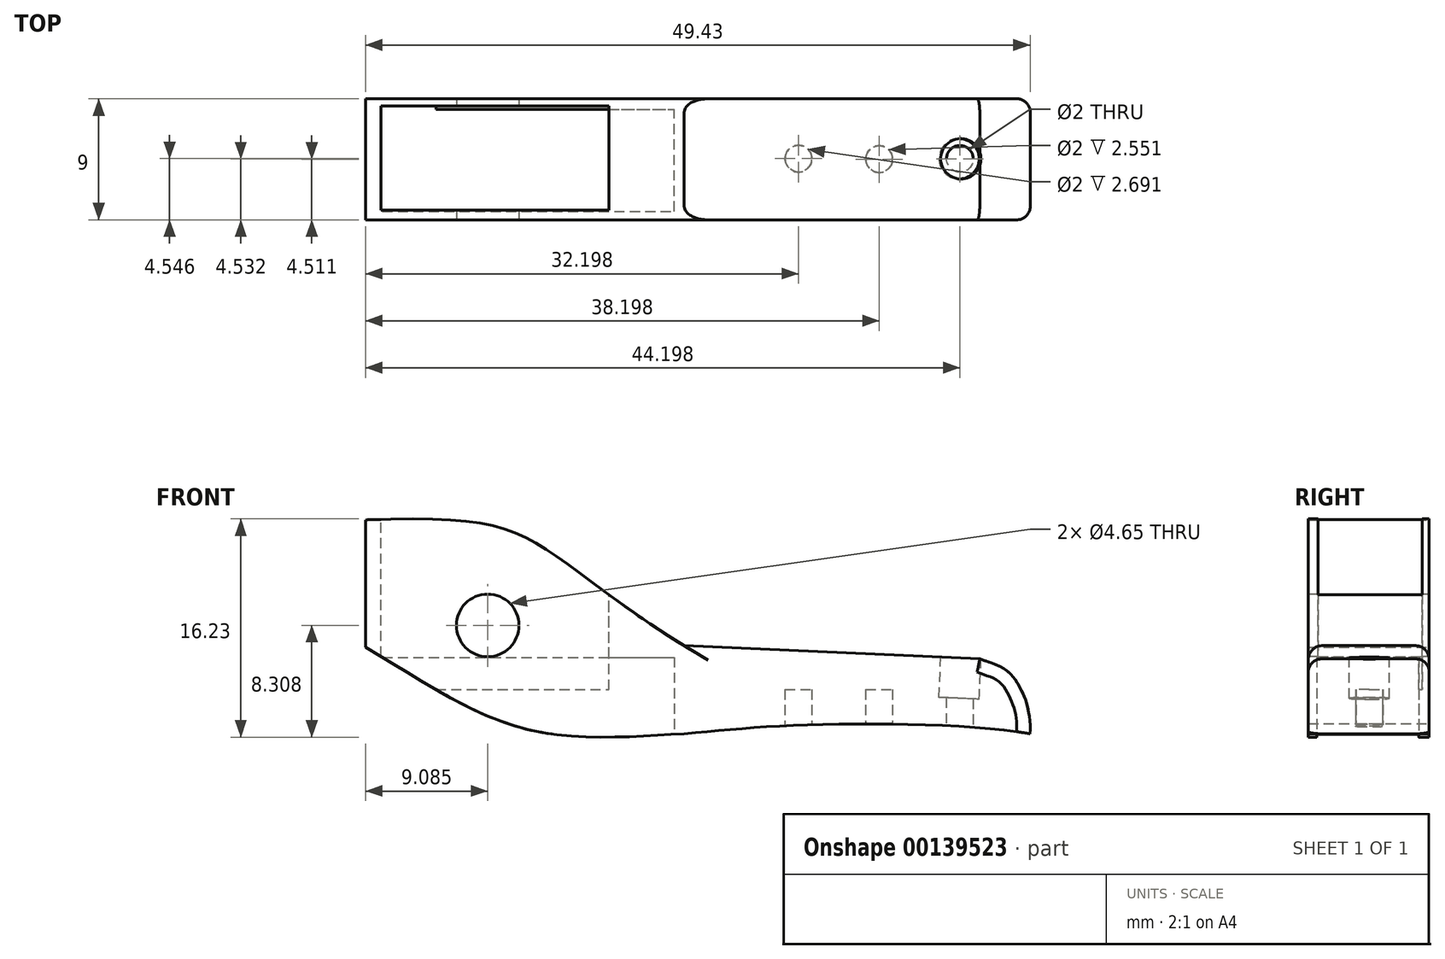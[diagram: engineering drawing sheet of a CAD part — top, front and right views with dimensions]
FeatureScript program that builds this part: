
annotation { "Feature Type Name" : "Feature", "Feature Type Description" : "" }
export const myFeature = defineFeature(function(context is Context, id is Id, definition is map)
    precondition{}
    {
        {
            var Q0;
            Q0=qCreatedBy(makeId("Front.planeOp"),FACE);
            var sketch = newSketch(context, id + "F0", { "sketchPlane" : qUnion([Q0])});
            skLineSegment(sketch, "E0", {"start": v(-18.11, 14.62) * mm, "end": v(-18.11, 5.15) * mm});
            skFitSpline(sketch, "E1", {"points": [v(-18.11, 14.62) * mm, v(-5.7, 13.04) * mm, v(5.6, 5.26) * mm], "startDerivative": vector(43.3, 1.46) * mm, "endDerivative": vector(32.79, -20.12) * mm});
            skFitSpline(sketch, "E2", {"points": [v(-18.11, 5.15) * mm, v(-6.1, -0.96) * mm, v(5.6, -1.29) * mm], "startDerivative": vector(24.76, -14.65) * mm, "endDerivative": vector(22.2, 1.12) * mm});
            skLineSegment(sketch, "E3", {"start": v(-5.7, 13.04) * mm, "end": v(-6.1, -0.96) * mm, "construction": true});
            skFitSpline(sketch, "E4", {"points": [v(5.6, -1.29) * mm, v(15.63, -0.6) * mm, v(31.3, -1.29) * mm], "startDerivative": vector(20.89, 1.84) * mm, "endDerivative": vector(17.9, -3.47) * mm});
            skLineSegment(sketch, "E5", {"start": v(5.6, 5.26) * mm, "end": v(27.57, 4.28) * mm});
            skFitSpline(sketch, "E6", {"points": [v(27.57, 4.28) * mm, v(30.02, 2.98) * mm, v(31.3, -1.29) * mm], "startDerivative": vector(8.93, -3.19) * mm, "endDerivative": vector(-1.08, -8.77) * mm});
            skLineSegment(sketch, "E7", {"start": v(-18.11, 14.62) * mm, "end": v(31.89, 14.62) * mm, "construction": true});
            skLineSegment(sketch, "E8", {"start": v(31.89, 14.62) * mm, "end": v(31.3, -1.29) * mm, "construction": true});
            skSolve(sketch);
        }
        {
            var Q0;
            Q0=qSketchRegion(id+"F0",true);
            extrude(context, id + "F1", {"entities" : qUnion([Q0]), "depth" : 9 * mm});
        }
        {
            var Q0;
            Q0=makeQuery(id+"F1.opExtrude","CAP_FACE",FACE,{"disambiguationData":[OSD([sQuery(id+"F0.wireOp",EDGE,"E0"),sQuery(id+"F0.wireOp",EDGE,"E1"),sQuery(id+"F0.wireOp",EDGE,"E2"),sQuery(id+"F0.wireOp",EDGE,"E4"),sQuery(id+"F0.wireOp",EDGE,"E5"),sQuery(id+"F0.wireOp",EDGE,"E6")])],"isStart":false});
            var sketch = newSketch(context, id + "F2", { "sketchPlane" : qUnion([Q0])});
            skCircle(sketch, "E9", {"center": v(-9.02, 6.77) * mm, "radius": 2.32 * mm});
            skSolve(sketch);
        }
        {
            var Q0;
            Q0=qSketchRegion(id+"F2",true);
            extrude(context, id + "F3", {"entities" : qUnion([Q0]), "operationType" : NewBodyOperationType.REMOVE, "oppositeDirection" : true, "depth" : 25 * mm});
        }
        {
            var Q0;
            Q0=makeQuery(id+"F1.opExtrude","CAP_EDGE",EDGE,{"disambiguationData":[OSD([sQuery(id+"F0.wireOp",EDGE,"E5")])],"isStart":false});
            var Q1;
            Q1=makeQuery(id+"F1.opExtrude","CAP_EDGE",EDGE,{"disambiguationData":[OSD([sQuery(id+"F0.wireOp",EDGE,"E5")])],"isStart":true});
            var Q2;
            Q2=makeQuery(id+"F1.opExtrude","CAP_EDGE",EDGE,{"disambiguationData":[OSD([sQuery(id+"F0.wireOp",EDGE,"E6")])],"isStart":false});
            var Q3;
            Q3=makeQuery(id+"F1.opExtrude","CAP_EDGE",EDGE,{"disambiguationData":[OSD([sQuery(id+"F0.wireOp",EDGE,"E6")])],"isStart":true});
            fillet(context, id + "F4", {"entities" : qUnion([Q0, Q1, Q2, Q3]), "radius" : 1 * mm, "tangentPropagation" : true, "allowEdgeOverflow" : false});
        }
        {
            var Q0;
            Q0=qCreatedBy(makeId("Top.planeOp"),FACE);
            cPlane(context, id + "F5", {"entities" : qUnion([Q0]), "cplaneType" : CPlaneType.OFFSET, "offset" : 3 * mm, "oppositeDirection" : true, "width" : 150 * mm, "height" : 150 * mm});
        }
        {
            var Q0;
            Q0=qCreatedBy(id+"F5.planeOp",FACE);
            cPlane(context, id + "F6", {"entities" : qUnion([Q0]), "cplaneType" : CPlaneType.OFFSET, "offset" : 25 * mm, "width" : 150 * mm, "height" : 150 * mm});
        }
        {
            var Q0;
            Q0=qCreatedBy(id+"F5.planeOp",FACE);
            var sketch = newSketch(context, id + "F7", { "sketchPlane" : qUnion([Q0])});
            skLineSegment(sketch, "E10.bottom", {"start": v(-17.4, -8.37) * mm, "end": v(4.86, -8.37) * mm});
            skLineSegment(sketch, "E10.top", {"start": v(-17.4, -0.78) * mm, "end": v(4.86, -0.78) * mm});
            skLineSegment(sketch, "E10.left", {"start": v(-17.4, -8.37) * mm, "end": v(-17.4, -0.78) * mm});
            skLineSegment(sketch, "E10.right", {"start": v(4.86, -8.37) * mm, "end": v(4.86, -0.78) * mm});
            skSolve(sketch);
        }
        {
            var Q0;
            Q0 = qSketchRegion(id + "F7", true);
            extrude(context, id + "F8", {"entities" : qUnion([Q0]), "operationType" : NewBodyOperationType.REMOVE, "depth" : 7.4 * mm});
        }
        {
            var Q0;
            Q0=qCreatedBy(id+"F6.planeOp",FACE);
            var sketch = newSketch(context, id + "F9", { "sketchPlane" : qUnion([Q0])});
            skLineSegment(sketch, "E11.bottom", {"start": v(-16.96, -0.52) * mm, "end": v(0, -0.52) * mm});
            skLineSegment(sketch, "E11.top", {"start": v(-16.96, -8.27) * mm, "end": v(0, -8.27) * mm});
            skLineSegment(sketch, "E11.left", {"start": v(-16.96, -0.52) * mm, "end": v(-16.96, -8.27) * mm});
            skLineSegment(sketch, "E11.right", {"start": v(0, -0.52) * mm, "end": v(0, -8.27) * mm});
            skPoint(sketch, "E11.middle", {"position": v(-8.48, -4.4) * mm});
            skSolve(sketch);
        }
        {
            var Q0;
            Q0 = qSketchRegion(id + "F9", true);
            extrude(context, id + "F10", {"entities" : qUnion([Q0]), "operationType" : NewBodyOperationType.REMOVE, "oppositeDirection" : true, "depth" : 20 * mm});
        }
        {
            var Q0;
            Q0=qCreatedBy(id+"F5.planeOp",FACE);
            var sketch = newSketch(context, id + "F11", { "sketchPlane" : qUnion([Q0])});
            skCircle(sketch, "E12", {"center": v(14.09, -4.45) * mm, "radius": 1 * mm});
            skCircle(sketch, "E13", {"center": v(20.09, -4.49) * mm, "radius": 1 * mm});
            skCircle(sketch, "E14", {"center": v(26.09, -4.47) * mm, "radius": 1 * mm});
            skLineSegment(sketch, "E15", {"start": v(5.59, -8.98) * mm, "end": v(5.59, 0) * mm, "construction": true});
            skLineSegment(sketch, "E16", {"start": v(5.59, 0) * mm, "end": v(5.59, -4.49) * mm, "construction": true});
            skLineSegment(sketch, "E17", {"start": v(5.59, -4.49) * mm, "end": v(34.6, -4.49) * mm, "construction": true});
            skLineSegment(sketch, "E18", {"start": v(26.09, -4.47) * mm, "end": v(31.59, -4.49) * mm, "construction": true});
            skSolve(sketch);
        }
        {
            var Q0;
            Q0 = qSketchRegion(id + "F11", true);
            extrude(context, id + "F12", {"entities" : qUnion([Q0]), "operationType" : NewBodyOperationType.REMOVE, "depth" : 5 * mm});
        }
        {
            var Q0;
            Q0=makeQuery(id+"F1.opExtrude","SWEPT_FACE",FACE,{"disambiguationData":[OSD([sQuery(id+"F0.wireOp",EDGE,"E5")])]});
            var sketch = newSketch(context, id + "F13", { "sketchPlane" : qUnion([Q0])});
            skLineSegment(sketch, "E19", {"start": v(30.95, 0) * mm, "end": v(30.95, -8.92) * mm, "construction": true});
            skLineSegment(sketch, "E20", {"start": v(30.95, -8.92) * mm, "end": v(30.95, -4.46) * mm, "construction": true});
            skLineSegment(sketch, "E21", {"start": v(30.95, -4.46) * mm, "end": v(7.42, -4.46) * mm, "construction": true});
            skCircle(sketch, "E22", {"center": v(25.95, -4.46) * mm, "radius": 1.5 * mm});
            skSolve(sketch);
        }
        {
            var Q0;
            Q0 = qSketchRegion(id + "F13", true);
            extrude(context, id + "F14", {"entities" : qUnion([Q0]), "operationType" : NewBodyOperationType.REMOVE, "oppositeDirection" : true, "depth" : 3 * mm});
        }
    });
